# Revit family: Studio-Patio-Door_OXYO-2.625-Sill
name_source: partatom
category: Doors
units: mm (PartAtom-declared; Revit-internal decimal feet)

## family parameters
Always vertical = Yes
Classification Number = 23.30.10.00
Cut with Voids When Loaded = No
Host = Wall
Room Calculation Point = No
Shared = No

## types (12) — shared parameters
Analytic Construction = <None>
Define Thermal Properties by = Schematic Type
Function = Interior
Glass = Glass
Height = 79.5 "
Height Sash = 76.125 "
Manufacturer = Novatech Group
Model = ƒif(([6p vs 7.25p]), "Urbania/Loft 6p", "Urbania/Loft 71/4p")
URL = https://www.groupenovatech.com
Wall Closure = By host
X2 = 75.924 "

## per-type parameters (varying)
| type | Door Width | Frame Material | Width | Width Sash | X1 |
| Custom Color - 189 1/2" × 79 1/2" | 96.5 " | Custom Color | 189.5 " | 48.25 " | 47.787 " |
| Custom Color - 141 1/2" × 79 1/2" | 72.5 " | Custom Color | 141.5 " | 36.25 " | 35.787 " |
| Custom Color - 117 1/2" × 79 1/2" | 60.5 " | Custom Color | 117.5 " | 30.25 " | 29.787 " |
| Clear anodized - 189 1/2" × 79 1/2" | 96.5 " | Clear anodized | 189.5 " | 48.25 " | 47.787 " |
| Clear anodized - 141 1/2" × 79 1/2" | 72.5 " | Clear anodized | 141.5 " | 36.25 " | 35.787 " |
| Clear anodized - 117 1/2" × 79 1/2" | 60.5 " | Clear anodized | 117.5 " | 30.25 " | 29.787 " |
| Black - 189 1/2" × 79 1/2" | 96.5 " | Black | 189.5 " | 48.25 " | 47.787 " |
| Black - 141 1/2" × 79 1/2" | 72.5 " | Black | 141.5 " | 36.25 " | 35.787 " |
| Black - 117 1/2" × 79 1/2" | 60.5 " | Black | 117.5 " | 30.25 " | 29.787 " |
| Commercial Brown - 189 1/2" × 79 1/2" | 96.5 " | Commercial Brown | 189.5 " | 48.25 " | 47.787 " |
| Commercial Brown - 141 1/2" × 79 1/2" | 72.5 " | Commercial Brown | 141.5 " | 36.25 " | 35.787 " |
| Commercial Brown - 117 1/2" × 79 1/2" | 60.5 " | Commercial Brown | 117.5 " | 30.25 " | 29.787 " |

## geometry (parser evidence)
native form markers: Sweep x8
no freeform markers — native parametric forms only
